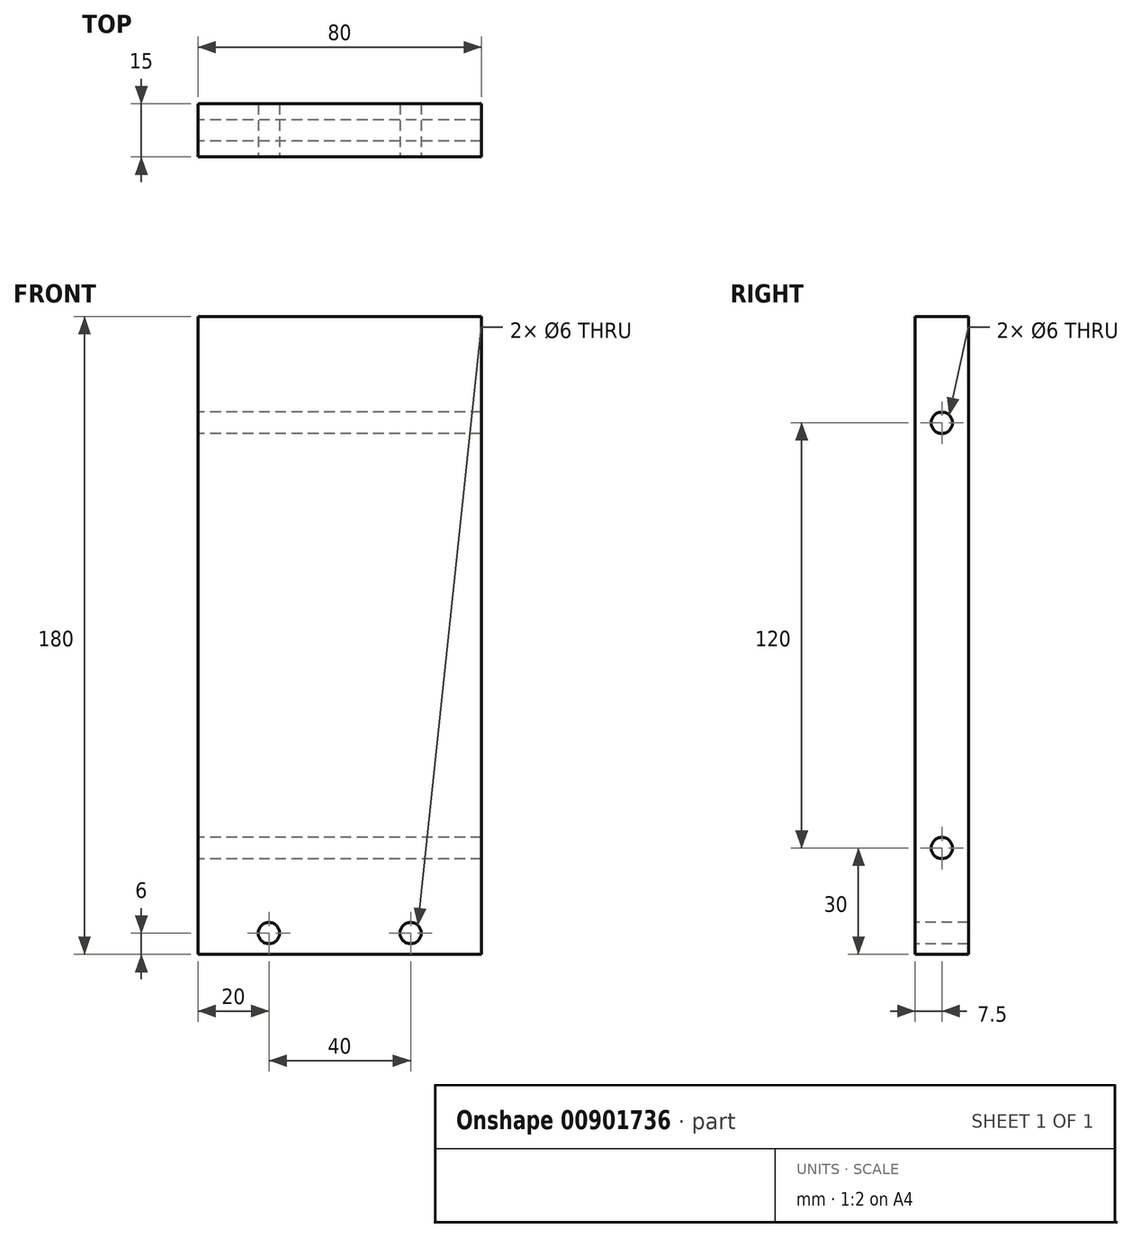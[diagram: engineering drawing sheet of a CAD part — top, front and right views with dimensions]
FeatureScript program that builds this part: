
annotation { "Feature Type Name" : "Feature", "Feature Type Description" : "" }
export const myFeature = defineFeature(function(context is Context, id is Id, definition is map)
    precondition{}
    {
        {
            var Q0;
            Q0=qCreatedBy(makeId("Front.planeOp"),FACE);
            var sketch = newSketch(context, id + "F0", { "sketchPlane" : qUnion([Q0])});
            skLineSegment(sketch, "E0.bottom", {"start": v(0, 0) * mm, "end": v(80, 0) * mm});
            skLineSegment(sketch, "E0.top", {"start": v(0, 180) * mm, "end": v(80, 180) * mm});
            skLineSegment(sketch, "E0.left", {"start": v(0, 0) * mm, "end": v(0, 180) * mm});
            skLineSegment(sketch, "E0.right", {"start": v(80, 0) * mm, "end": v(80, 180) * mm});
            skSolve(sketch);
        }
        {
            var Q0;
            Q0 = qSketchRegion(id + "F0", true);
            extrude(context, id + "F1", {"entities" : qUnion([Q0]), "depth" : 15 * mm, "offsetDistance" : 25 * mm});
        }
        {
            var Q0;
            Q0=makeQuery(id+"F1.opExtrude","CAP_FACE",FACE,{"disambiguationData":[OSD([sQuery(id+"F0.wireOp",EDGE,"E0.bottom"),sQuery(id+"F0.wireOp",EDGE,"E0.top"),sQuery(id+"F0.wireOp",EDGE,"E0.left"),sQuery(id+"F0.wireOp",EDGE,"E0.right")])],"isStart":false});
            var sketch = newSketch(context, id + "F2", { "sketchPlane" : qUnion([Q0])});
            skCircle(sketch, "E1", {"center": v(60, 6) * mm, "radius": 3 * mm});
            skCircle(sketch, "E2", {"center": v(20, 6) * mm, "radius": 3 * mm});
            skSolve(sketch);
        }
        {
            var Q0;
            Q0 = qSketchRegion(id + "F2", true);
            extrude(context, id + "F3", {"entities" : qUnion([Q0]), "operationType" : NewBodyOperationType.REMOVE, "endBound" : BoundingType.THROUGH_ALL, "oppositeDirection" : true, "depth" : 25 * mm, "offsetDistance" : 25 * mm});
        }
        {
            var Q0;
            Q0=makeQuery(id+"F1.opExtrude","SWEPT_FACE",FACE,{"disambiguationData":[OSD([sQuery(id+"F0.wireOp",EDGE,"E0.left")])]});
            var sketch = newSketch(context, id + "F4", { "sketchPlane" : qUnion([Q0])});
            skCircle(sketch, "E3", {"center": v(7.5, 30) * mm, "radius": 3 * mm});
            skCircle(sketch, "E4", {"center": v(7.5, 150) * mm, "radius": 3 * mm});
            skSolve(sketch);
        }
        {
            var Q0;
            Q0 = qSketchRegion(id + "F4", true);
            extrude(context, id + "F5", {"entities" : qUnion([Q0]), "operationType" : NewBodyOperationType.REMOVE, "endBound" : BoundingType.THROUGH_ALL, "oppositeDirection" : true, "depth" : 25 * mm, "offsetDistance" : 25 * mm});
        }
    });
